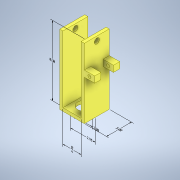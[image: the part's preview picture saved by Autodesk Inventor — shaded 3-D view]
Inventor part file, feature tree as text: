
AUTODESK INVENTOR PART (.ipt)
format: ipt  version: 2021.2 (Build 252289000, 289)  size: 169,472 bytes
history: native  units: in
note: dims shown in document units (in); Inventor stores cm internally (conversion verified against a paired STEP export)
features: other x6, extrude x4, sketch x4, mirror x1
ambient origin geometry x8: Origin, YZ Plane, XZ Plane, XY Plane, X Axis, Y Axis, Z Axis, Center Point
bodies: Solid1 (feature_tree)
feature tree (15):
  other  "Annotations"
  extrude  "Extrusion1"  Depth=1.1in
  extrude  "Extrusion2"  Depth=0.375in
  extrude  "Extrusion3"  Depth=3.0in
  mirror  "Mirror1"
  extrude  "Extrusion4"  TaperAngle=0.0deg  [1 undecoded]
  sketch  "Sketch1"  dims[d0=8.0in d1=1.1in]
  sketch  "Sketch2"  dims[d3=0.375in d4=0.375in]
  sketch  "Sketch3"  dims[d5=3.0in d6=0.0in d7=0.625in]
  sketch  "Sketch4"  dims[d8=7.5in d9=0.0in d10=0.0in d20=1.25in d21=0.75in d22=5.215in d23=0.375in d24=0.617in d25=0.75in d26=0.0in d27=1.625in d28=0.0in d29=0.0in d11=0.2367in d12=0.1768in d13=2.2in d14=0.3014in d15=0.1709in d16=2.95in d17=0.0in d18=0.3937in d19=3.0in d30=0.0192in d31=2.2in d32=0.2345in d33=0.0621in d34=8.375in]
  other  "Linear Dimension 1"
  other  "Linear Dimension 2"
  other  "Linear Dimension 3"
  other  "Linear Dimension 4"
  other  "Linear Dimension 5"
note: 1 required parameter value undecoded (feature->parameter linkage not recoverable at this tier; creation-order binding heuristic only, values carry confidence <= 0.55)
